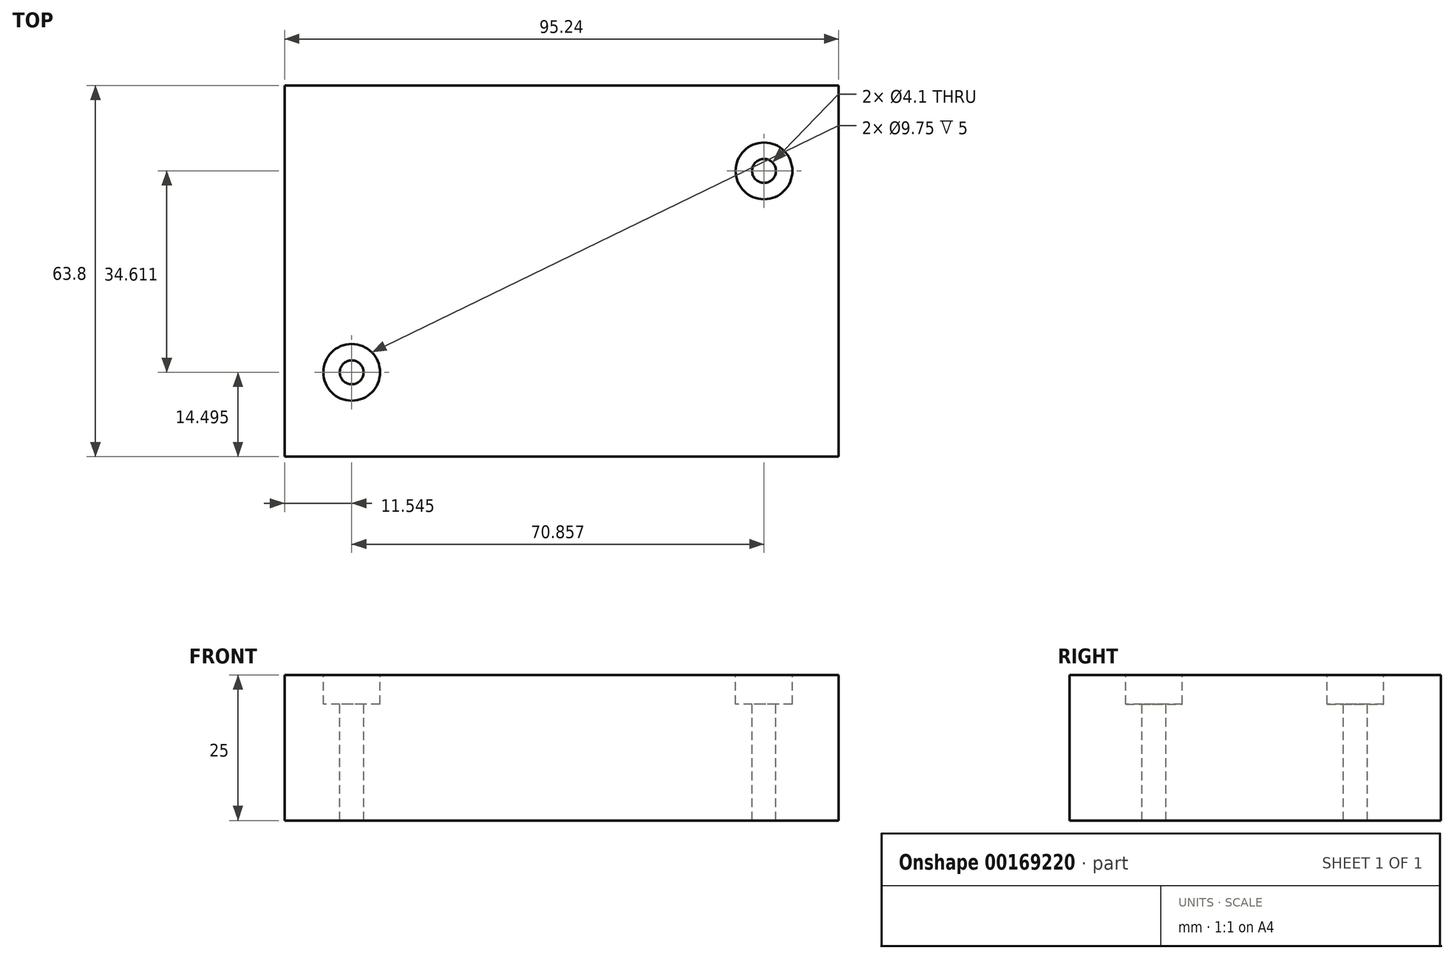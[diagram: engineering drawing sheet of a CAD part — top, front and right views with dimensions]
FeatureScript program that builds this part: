
annotation { "Feature Type Name" : "Feature", "Feature Type Description" : "" }
export const myFeature = defineFeature(function(context is Context, id is Id, definition is map)
    precondition{}
    {
        {
            var Q0;
            Q0=qCreatedBy(makeId("Top.planeOp"),FACE);
            var sketch = newSketch(context, id + "F0", { "sketchPlane" : qUnion([Q0])});
            skLineSegment(sketch, "E0.bottom", {"start": v(47.62, -31.9) * mm, "end": v(-47.62, -31.9) * mm});
            skLineSegment(sketch, "E0.top", {"start": v(47.62, 31.9) * mm, "end": v(-47.62, 31.9) * mm});
            skLineSegment(sketch, "E0.left", {"start": v(47.62, -31.9) * mm, "end": v(47.62, 31.9) * mm});
            skLineSegment(sketch, "E0.right", {"start": v(-47.62, -31.9) * mm, "end": v(-47.62, 31.9) * mm});
            skPoint(sketch, "E0.middle", {"position": v(0, 0) * mm});
            skSolve(sketch);
        }
        {
            var Q0;
            Q0 = qSketchRegion(id + "F0", true);
            extrude(context, id + "F1", {"entities" : qUnion([Q0]), "depth" : 25 * mm});
        }
        {
            var Q0;
            Q0=makeQuery(id+"F1.opExtrude","CAP_FACE",FACE,{"disambiguationData":[OSD([sQuery(id+"F0.wireOp",EDGE,"E0.bottom"),sQuery(id+"F0.wireOp",EDGE,"E0.top"),sQuery(id+"F0.wireOp",EDGE,"E0.left"),sQuery(id+"F0.wireOp",EDGE,"E0.right")])],"isStart":false});
            var sketch = newSketch(context, id + "F2", { "sketchPlane" : qUnion([Q0])});
            skPoint(sketch, "E1", {"position": v(-36.07, -17.4) * mm});
            skSolve(sketch);
        }
        {
            var Q0;
            Q0=sQuery(id+"F2.wireOp",VERTEX,"E1");
            var Q1;
            Q1=makeQuery(id+"F1.opExtrude","SWEPT_BODY",BODY,{"disambiguationData":[OSD([sQuery(id+"F0.wireOp",EDGE,"E0.bottom"),sQuery(id+"F0.wireOp",EDGE,"E0.top"),sQuery(id+"F0.wireOp",EDGE,"E0.left"),sQuery(id+"F0.wireOp",EDGE,"E0.right")])]});
            hole(context, id + "F3", {"style" : HoleStyle.C_BORE, "endStyle" : HoleEndStyle.THROUGH, "standardTappedOrClearance" : lookupTablePath({ "standard" : "ISO", "engagement" : "75%", "pitch" : "0.9 mm", "size" : "M5", "type" : "Tapped" }), "standardBlindInLast" : lookupTablePath({ "standard" : "ISO", "engagement" : "75%", "pitch" : "0.9 mm", "size" : "M5", "type" : "Tapped" }), "holeDiameter" : 4.1 * mm, "cBoreDiameter" : 9.75 * mm, "cBoreDepth" : 5 * mm, "locations" : qUnion([Q0]), "scope" : qUnion([Q1]), "isTappedThrough" : true, "showTappedDepth" : true});
        }
        {
            var Q0;
            Q0=makeQuery(id+"F1.opExtrude","CAP_FACE",FACE,{"disambiguationData":[OSD([sQuery(id+"F0.wireOp",EDGE,"E0.bottom"),sQuery(id+"F0.wireOp",EDGE,"E0.top"),sQuery(id+"F0.wireOp",EDGE,"E0.left"),sQuery(id+"F0.wireOp",EDGE,"E0.right")])],"isStart":false});
            var sketch = newSketch(context, id + "F4", { "sketchPlane" : qUnion([Q0])});
            skPoint(sketch, "E2", {"position": v(34.78, 17.2) * mm});
            skSolve(sketch);
        }
        {
            var Q0;
            Q0=sQuery(id+"F4.wireOp",VERTEX,"E2");
            var Q1;
            Q1=makeQuery(id+"F1.opExtrude","SWEPT_BODY",BODY,{"disambiguationData":[OSD([sQuery(id+"F0.wireOp",EDGE,"E0.bottom"),sQuery(id+"F0.wireOp",EDGE,"E0.top"),sQuery(id+"F0.wireOp",EDGE,"E0.left"),sQuery(id+"F0.wireOp",EDGE,"E0.right")])]});
            hole(context, id + "F5", {"style" : HoleStyle.C_BORE, "endStyle" : HoleEndStyle.THROUGH, "standardTappedOrClearance" : lookupTablePath({ "standard" : "ISO", "engagement" : "75%", "pitch" : "0.9 mm", "size" : "M5", "type" : "Tapped" }), "standardBlindInLast" : lookupTablePath({ "standard" : "ISO", "engagement" : "75%", "pitch" : "0.9 mm", "size" : "M5", "type" : "Tapped" }), "holeDiameter" : 4.1 * mm, "cBoreDiameter" : 9.75 * mm, "cBoreDepth" : 5 * mm, "locations" : qUnion([Q0]), "scope" : qUnion([Q1]), "isTappedThrough" : true, "showTappedDepth" : true});
        }
    });
